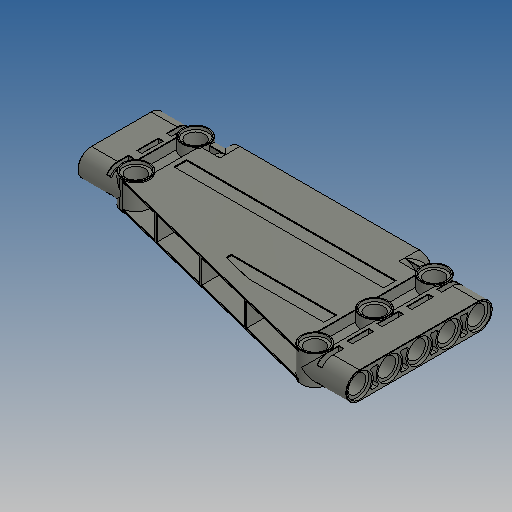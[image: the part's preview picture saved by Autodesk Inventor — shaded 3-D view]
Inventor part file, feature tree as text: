
AUTODESK INVENTOR PART (.ipt)
format: ipt  version: 2025 (Build 290162010, 162A)  size: 1,147,904 bytes
history: native  units: in
note: dims shown in document units (in); Inventor stores cm internally (conversion verified against a paired STEP export)
features: extrude x26, sketch x6, projected_geometry x2, plane x1, mirror x1, fillet x1
ambient origin geometry x8: Origin, YZ Plane, XZ Plane, XY Plane, X Axis, Y Axis, Z Axis, Center Point
bodies: Solid3 (feature_tree)
feature tree (37):
  sketch  "Sketch3"  dims[d15=0.189in d16=2.5197in]
  extrude  "Extrusion3"  Depth=0.252in
  plane  "Work Plane1"
  sketch  "Sketch2"  dims[d13=0.2835in d14=0.252in]
  extrude  "Extrusion6"  Depth=2.5197in
  extrude  "Extrusion8"  TaperAngle=45.0deg  [1 undecoded]
  extrude  "Extrusion9"  TaperAngle=0.0deg  [1 undecoded]
  extrude  "Extrusion10"  TaperAngle=0.0deg  [1 undecoded]
  extrude  "Extrusion11"  TaperAngle=0.0deg  [1 undecoded]
  extrude  "Extrusion7"  Depth=0.3937in TaperAngle=0.0deg
  extrude  "Extrusion12"  Depth=0.0157in TaperAngle=0.0deg
  extrude  "Extrusion4"  Depth=0.0157in
  sketch  "Sketch5"  dims[d19=0.2835in d20=0.0in]
  extrude  "Extrusion13"  TaperAngle=0.0deg  [1 undecoded]
  extrude  "Extrusion14"  Depth=0.0157in
  extrude  "Extrusion15"  TaperAngle=0.0deg  [1 undecoded]
  extrude  "Extrusion16"  Depth=0.2205in TaperAngle=0.0deg
  extrude  "Extrusion17"  Depth=0.2205in TaperAngle=0.0deg
  extrude  "Extrusion18"  Depth=0.2205in TaperAngle=0.0deg
  sketch  "Sketch6"  dims[d21=0.063in d22=0.0in]
  extrude  "Extrusion21"  Depth=0.0157in
  extrude  "Extrusion22"  Depth=0.2205in TaperAngle=0.0deg
  extrude  "Extrusion23"  Depth=0.0157in
  extrude  "Extrusion24"  Depth=0.0157in
  extrude  "Extrusion25"  TaperAngle=45.0deg  [1 undecoded]
  extrude  "Extrusion26"  Depth=0.0157in TaperAngle=0.0deg
  extrude  "Extrusion5"  Depth=0.0157in TaperAngle=0.0deg
  extrude  "Extrusion19"  Depth=0.0157in TaperAngle=0.0deg
  extrude  "Extrusion20"  Depth=0.0157in TaperAngle=0.0deg
  sketch  "Sketch7"  dims[d23=0.315in d24=0.0in d37=0.3937in d38=0.0in d39=0.2117in d40=0.0in d41=0.2835in d42=0.0in d43=0.0315in d44=0.0in d45=0.2205in d46=0.0in d47=0.2205in d48=0.0in d49=0.2205in d50=0.0in d51=0.2835in d52=0.2205in d53=0.0in d54=0.252in d55=0.189in d56=45.0deg d57=0.3723in d58=0.0in d59=0.0416in d60=0.0in d61=0.3408in d62=0.0in d63=0.1518in d64=0.0in d65=0.1518in d66=0.0in d67=0.1518in d68=0.0in d69=0.252in d70=0.0in d71=0.2835in d72=0.252in d73=0.189in d74=45.0deg d75=0.252in d76=0.0in d77=0.252in d78=0.0in d79=0.3723in d80=0.0in d81=0.0416in d82=0.0in d83=0.3408in d84=0.0in d85=0.1518in d86=0.0in d87=-0.7874in d88=0.315in d89=0.189in d90=0.2441in d93=0.0315in d94=0.0315in d95=0.0315in d100=45.0deg d101=0.0416in d102=0.0416in d103=0.0472in d104=0.2205in d105=2.2047in d106=0.4094in d107=0.126in d108=0.5039in d109=1.1024in d110=0.0487in d111=0.0079in d112=0.0in d113=0.0079in d114=0.0in d115=0.0039in d116=0.0157in]
  extrude  "Extrusion27"  Depth=0.0157in TaperAngle=0.0deg
  mirror  "Mirror1"
  extrude  "Extrusion28"  Depth=0.0157in TaperAngle=0.0deg
  fillet  "Fillet1"  Radius=0.252in
  sketch  "Sketch4"  dims[d17=0.6299in d18=45.0deg]
  projected_geometry  "Projected Loop1"
  projected_geometry  "Projected Loop2"
note: 7 required parameter values undecoded (feature->parameter linkage not recoverable at this tier; creation-order binding heuristic only, values carry confidence <= 0.55)
